# Revit family: SW01 AART
name_source: partatom
category: Detail Items
units: mm (PartAtom-declared; Revit-internal decimal feet)

## family parameters
Rotate with component = No
Section Shape = Not Defined
Shared = No

## types (4) — shared parameters
URL = www.superwood.dk

## per-type parameters (varying)
| type | 0 spor | 1 spor | 2 spor | Afstand til første spor | Afstandmellem spor | h |
| SW01 AART 3" - 21x70mm | Yes | No | No | 36 mm  [stored 0.11811 ft] | 2 mm  [stored 0.00656168 ft] | 70 mm  [stored 0.229659 ft] |
| SW01 AART 4" - 21x95mm | No | Yes | No | 36 mm  [stored 0.11811 ft] | 2 mm  [stored 0.00656168 ft] | 95 mm |
| SW01 AART 5" - 21x120mm | No | No | Yes | 26 mm | 36.8 mm  [stored 0.120735 ft] | 120 mm  [stored 0.393701 ft] |
| SW01 AART 6" - 21x145mm | No | No | Yes | 36 mm  [stored 0.11811 ft] | 36.8 mm  [stored 0.120735 ft] | 145 mm  [stored 0.475722 ft] |

note: [stored X ft] marks values corroborated as IEEE doubles in the binary element streams (Revit-internal decimal feet)

## geometry (parser evidence)
native form markers: Sweep x1
no freeform markers — native parametric forms only
